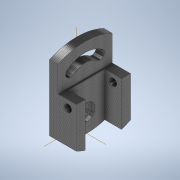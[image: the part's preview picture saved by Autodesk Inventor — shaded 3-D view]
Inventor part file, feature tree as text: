
AUTODESK INVENTOR PART (.ipt)
format: ipt  version: 2021.1 (Build 251245000, 245)  size: 168,960 bytes
history: native  units: in
note: dims shown in document units (in); Inventor stores cm internally (conversion verified against a paired STEP export)
features: sketch x5, extrude x4, hole x1
ambient origin geometry x8: Origin, YZ Plane, XZ Plane, XY Plane, X Axis, Y Axis, Z Axis, Center Point
bodies: Solid1 (feature_tree)
feature tree (10):
  extrude  "Extrusion1"  Depth=4.252in
  extrude  "Extrusion2"  Depth=3.8189in
  extrude  "Extrusion3"  Depth=0.315in
  extrude  "Extrusion4"  Depth=1.8898in
  hole  "Hole1"  [1 undecoded]
  sketch  "Sketch1"  dims[d0=4.252in d2=5.5512in]
  sketch  "Sketch2"  dims[d3=3.8189in d4=2.126in]
  sketch  "Sketch3"  dims[d5=0.315in d6=1.7717in]
  sketch  "Sketch4"  dims[d7=1.8898in d8=0.0in d9=3.3071in]
  sketch  "Sketch5"  dims[d10=1.2992in d11=0.0in d12=0.6299in d13=0.6299in d14=1.1811in d15=0.0in d16=0.5118in d17=0.5118in d18=0.5906in d19=1.1811in d20=0.0in d21=1.2992in d22=0.8268in d23=1.1024in d24=1.1811in d25=0.2362in d26=0.5635in d27=1.3031in d28=0.8108in]
note: 1 required parameter value undecoded (feature->parameter linkage not recoverable at this tier; creation-order binding heuristic only, values carry confidence <= 0.55)
